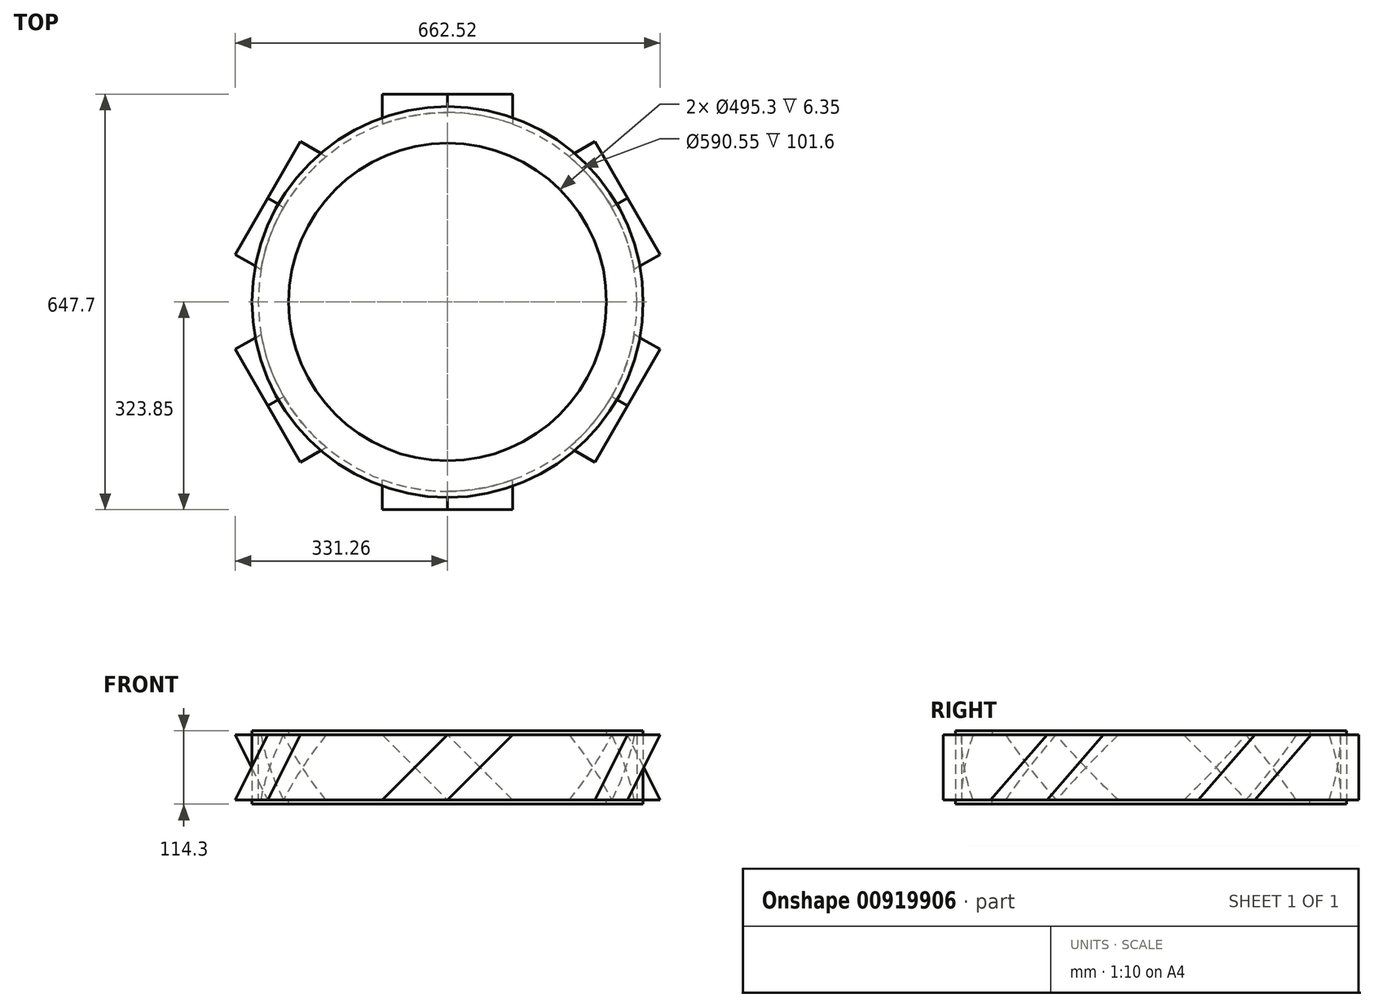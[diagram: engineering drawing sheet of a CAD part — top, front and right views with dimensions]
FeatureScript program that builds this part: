
annotation { "Feature Type Name" : "Feature", "Feature Type Description" : "" }
export const myFeature = defineFeature(function(context is Context, id is Id, definition is map)
    precondition{}
    {
        {
            var Q0;
            Q0=qCreatedBy(makeId("Top.planeOp"),FACE);
            var sketch = newSketch(context, id + "F0", { "sketchPlane" : qUnion([Q0])});
            skCircle(sketch, "E0", {"center": v(0, 0) * mm, "radius": 304.8 * mm});
            skCircle(sketch, "E1", {"center": v(0, 0) * mm, "radius": 295.28 * mm});
            skLineSegment(sketch, "E2", {"start": v(-528.88, -206.99) * mm, "end": v(-528.88, 98.57) * mm});
            skLineSegment(sketch, "E3", {"start": v(-528.88, 98.57) * mm, "end": v(-565.97, 49.3) * mm});
            skLineSegment(sketch, "E4", {"start": v(-565.97, 49.3) * mm, "end": v(-528.88, 98.57) * mm});
            skLineSegment(sketch, "E5", {"start": v(-528.88, 98.57) * mm, "end": v(-477.58, 49.3) * mm});
            skSolve(sketch);
        }
        {
            var Q0;
            Q0=makeQuery(id+"F0.imprint","IMPRINT",FACE,{"disambiguationData":[TD([[makeQuery(id+"F0.imprint","IMPRINT",EDGE,{"derivedFrom":sQuery(id+"F0.wireOp",EDGE,"E0")}),1.0]])]});
            extrude(context, id + "F1", {"entities" : qUnion([Q0]), "depth" : 101.6 * mm, "offsetDistance" : 25.4 * mm});
        }
        {
            var Q0;
            Q0=qCreatedBy(makeId("Front.planeOp"),FACE);
            var sketch = newSketch(context, id + "F2", { "sketchPlane" : qUnion([Q0])});
            skLineSegment(sketch, "E6", {"start": v(0, 0) * mm, "end": v(101.6, 0) * mm});
            skLineSegment(sketch, "E7", {"start": v(101.6, 0) * mm, "end": v(0, 101.6) * mm});
            skLineSegment(sketch, "E8", {"start": v(0, 101.6) * mm, "end": v(-101.6, 101.6) * mm});
            skLineSegment(sketch, "E9", {"start": v(-101.6, 101.6) * mm, "end": v(0, 0) * mm});
            skLineSegment(sketch, "E10", {"start": v(0, 101.6) * mm, "end": v(0, 0) * mm});
            skSolve(sketch);
        }
        {
            var Q0;
            Q0=makeQuery(id+"F2.imprint","IMPRINT",FACE,{"disambiguationData":[TD([[makeQuery(id+"F2.imprint","IMPRINT",EDGE,{"derivedFrom":sQuery(id+"F2.wireOp",EDGE,"E6")}),1.0]])]});
            var Q1;
            Q1=makeQuery(id+"F2.imprint","IMPRINT",FACE,{"disambiguationData":[TD([[makeQuery(id+"F2.imprint","IMPRINT",EDGE,{"derivedFrom":sQuery(id+"F2.wireOp",EDGE,"E8")}),1.0]])]});
            extrude(context, id + "F3", {"entities" : qUnion([Q0, Q1]), "oppositeDirection" : true, "depth" : 323.85 * mm, "offsetDistance" : 25.4 * mm});
        }
        {
            var Q0;
            Q0=makeQuery(id+"F0.imprint","IMPRINT",FACE,{"disambiguationData":[TD([[makeQuery(id+"F0.imprint","IMPRINT",EDGE,{"derivedFrom":sQuery(id+"F0.wireOp",EDGE,"E1")}),1.0]])]});
            extrude(context, id + "F4", {"entities" : qUnion([Q0]), "operationType" : NewBodyOperationType.REMOVE, "depth" : 254 * mm, "offsetDistance" : 25.4 * mm});
        }
        {
            var Q0;
            Q0=makeQuery(id+"F3.opExtrude","SWEPT_BODY",BODY,{"disambiguationData":[OSD([sQuery(id+"F2.wireOp",EDGE,"E6"),sQuery(id+"F2.wireOp",EDGE,"E7"),sQuery(id+"F2.wireOp",EDGE,"E8"),sQuery(id+"F2.wireOp",EDGE,"E9")])]});
            var Q1;
            Q1=sQuery(id+"F2.wireOp",EDGE,"E10");
            circularPattern(context, id + "F5", {"entities" : qUnion([Q0]), "axis" : qUnion([Q1]), "angle" : 360 * degree, "instanceCount" : 6, "equalSpace" : true});
        }
        {
            var Q0;
            Q0=makeQuery(id+"F0.imprint","IMPRINT",FACE,{"disambiguationData":[TD([[makeQuery(id+"F0.imprint","IMPRINT",EDGE,{"derivedFrom":sQuery(id+"F0.wireOp",EDGE,"E0")}),1.0]])]});
            var Q1;
            Q1=makeQuery(id+"F5.opPattern","COPY",FACE,{"derivedFrom":makeQuery(id+"F3.opExtrude","SWEPT_FACE",FACE,{"disambiguationData":[OSD([sQuery(id+"F2.wireOp",EDGE,"fI1UZwbh-BgUO-eOab-QM0r-AAAHP5eAAkyZ")])]}),"instanceName":"7"});
            var Q2;
            Q2=makeQuery(id+"F5.opPattern","COPY",FACE,{"derivedFrom":makeQuery(id+"F3.opExtrude","SWEPT_FACE",FACE,{"disambiguationData":[OSD([sQuery(id+"F2.wireOp",EDGE,"fI1UZwbh-BgUO-eOab-QM0r-AAAHP5eAAkyZ")])]}),"instanceName":"6"});
            var Q3;
            Q3=makeQuery(id+"F5.opPattern","COPY",FACE,{"derivedFrom":makeQuery(id+"F3.opExtrude","SWEPT_FACE",FACE,{"disambiguationData":[OSD([sQuery(id+"F2.wireOp",EDGE,"fI1UZwbh-BgUO-eOab-QM0r-AAAHP5eAAkyZ")])]}),"instanceName":"5"});
            var Q4;
            Q4=makeQuery(id+"F5.opPattern","COPY",FACE,{"derivedFrom":makeQuery(id+"F3.opExtrude","SWEPT_FACE",FACE,{"disambiguationData":[OSD([sQuery(id+"F2.wireOp",EDGE,"fI1UZwbh-BgUO-eOab-QM0r-AAAHP5eAAkyZ")])]}),"instanceName":"4"});
            var Q5;
            Q5=makeQuery(id+"F3.opExtrude","SWEPT_FACE",FACE,{"disambiguationData":[OSD([sQuery(id+"F2.wireOp",EDGE,"fI1UZwbh-BgUO-eOab-QM0r-AAAHP5eAAkyZ")])]});
            var Q6;
            Q6=makeQuery(id+"F5.opPattern","COPY",FACE,{"derivedFrom":makeQuery(id+"F3.opExtrude","SWEPT_FACE",FACE,{"disambiguationData":[OSD([sQuery(id+"F2.wireOp",EDGE,"fI1UZwbh-BgUO-eOab-QM0r-AAAHP5eAAkyZ")])]}),"instanceName":"1"});
            var Q7;
            Q7=makeQuery(id+"F5.opPattern","COPY",FACE,{"derivedFrom":makeQuery(id+"F3.opExtrude","SWEPT_FACE",FACE,{"disambiguationData":[OSD([sQuery(id+"F2.wireOp",EDGE,"fI1UZwbh-BgUO-eOab-QM0r-AAAHP5eAAkyZ")])]}),"instanceName":"2"});
            var Q8;
            Q8=makeQuery(id+"F5.opPattern","COPY",FACE,{"derivedFrom":makeQuery(id+"F3.opExtrude","SWEPT_FACE",FACE,{"disambiguationData":[OSD([sQuery(id+"F2.wireOp",EDGE,"fI1UZwbh-BgUO-eOab-QM0r-AAAHP5eAAkyZ")])]}),"instanceName":"3"});
            var Q9;
            Q9=makeQuery(id+"F0.imprint","IMPRINT",FACE,{"disambiguationData":[TD([[makeQuery(id+"F0.imprint","IMPRINT",EDGE,{"derivedFrom":sQuery(id+"F0.wireOp",EDGE,"E1")}),1.0]])]});
            extrude(context, id + "F6", {"entities" : qUnion([Q0, Q1, Q2, Q3, Q4, Q5, Q6, Q7, Q8, Q9]), "oppositeDirection" : true, "depth" : 6.35 * mm, "offsetDistance" : 25.4 * mm});
        }
        {
            var Q0;
            Q0=makeQuery(id+"F1.opExtrude","CAP_FACE",FACE,{"disambiguationData":[OSD([sQuery(id+"F0.wireOp",EDGE,"E0"),sQuery(id+"F0.wireOp",EDGE,"E1")])],"isStart":false});
            var sketch = newSketch(context, id + "F7", { "sketchPlane" : qUnion([Q0])});
            skCircle(sketch, "E11", {"center": v(0, 0) * mm, "radius": 247.65 * mm});
            skCircle(sketch, "E12", {"center": v(0, 0) * mm, "radius": 304.8 * mm});
            skSolve(sketch);
        }
        {
            var Q0;
            Q0=makeQuery(id+"F7.imprint","IMPRINT",FACE,{"disambiguationData":[TD([[makeQuery(id+"F7.imprint","IMPRINT",EDGE,{"derivedFrom":sQuery(id+"F7.wireOp",EDGE,"E11")}),-1.0]])]});
            var Q1;
            Q1=makeQuery(id+"F7.imprint","IMPRINT",FACE,{"disambiguationData":[TD([[makeQuery(id+"F7.imprint","IMPRINT",EDGE,{"derivedFrom":sQuery(id+"F7.wireOp",EDGE,"E12")}),1.0]])]});
            var Q2;
            Q2=makeQuery(id+"F5.opPattern","COPY",FACE,{"derivedFrom":makeQuery(id+"F3.opExtrude","SWEPT_FACE",FACE,{"disambiguationData":[OSD([sQuery(id+"F2.wireOp",EDGE,"ouPGAYGL-9uzs-f7dU-DYR0-UCYUhEhHpE3X")])]}),"instanceName":"6"});
            var Q3;
            Q3=makeQuery(id+"F5.opPattern","COPY",FACE,{"derivedFrom":makeQuery(id+"F3.opExtrude","SWEPT_FACE",FACE,{"disambiguationData":[OSD([sQuery(id+"F2.wireOp",EDGE,"ouPGAYGL-9uzs-f7dU-DYR0-UCYUhEhHpE3X")])]}),"instanceName":"5"});
            var Q4;
            Q4=makeQuery(id+"F5.opPattern","COPY",FACE,{"derivedFrom":makeQuery(id+"F3.opExtrude","SWEPT_FACE",FACE,{"disambiguationData":[OSD([sQuery(id+"F2.wireOp",EDGE,"ouPGAYGL-9uzs-f7dU-DYR0-UCYUhEhHpE3X")])]}),"instanceName":"3"});
            var Q5;
            Q5=makeQuery(id+"F5.opPattern","COPY",FACE,{"derivedFrom":makeQuery(id+"F3.opExtrude","SWEPT_FACE",FACE,{"disambiguationData":[OSD([sQuery(id+"F2.wireOp",EDGE,"ouPGAYGL-9uzs-f7dU-DYR0-UCYUhEhHpE3X")])]}),"instanceName":"2"});
            var Q6;
            Q6=makeQuery(id+"F3.opExtrude","SWEPT_FACE",FACE,{"disambiguationData":[OSD([sQuery(id+"F2.wireOp",EDGE,"ouPGAYGL-9uzs-f7dU-DYR0-UCYUhEhHpE3X")])]});
            var Q7;
            Q7=makeQuery(id+"F5.opPattern","COPY",FACE,{"derivedFrom":makeQuery(id+"F3.opExtrude","SWEPT_FACE",FACE,{"disambiguationData":[OSD([sQuery(id+"F2.wireOp",EDGE,"ouPGAYGL-9uzs-f7dU-DYR0-UCYUhEhHpE3X")])]}),"instanceName":"7"});
            var Q8;
            Q8=makeQuery(id+"F5.opPattern","COPY",FACE,{"derivedFrom":makeQuery(id+"F3.opExtrude","SWEPT_FACE",FACE,{"disambiguationData":[OSD([sQuery(id+"F2.wireOp",EDGE,"ouPGAYGL-9uzs-f7dU-DYR0-UCYUhEhHpE3X")])]}),"instanceName":"1"});
            var Q9;
            Q9=makeQuery(id+"F5.opPattern","COPY",FACE,{"derivedFrom":makeQuery(id+"F3.opExtrude","SWEPT_FACE",FACE,{"disambiguationData":[OSD([sQuery(id+"F2.wireOp",EDGE,"ouPGAYGL-9uzs-f7dU-DYR0-UCYUhEhHpE3X")])]}),"instanceName":"4"});
            extrude(context, id + "F8", {"entities" : qUnion([Q0, Q1, Q2, Q3, Q4, Q5, Q6, Q7, Q8, Q9]), "depth" : 6.35 * mm, "offsetDistance" : 25.4 * mm});
        }
        {
            var Q0;
            Q0=makeQuery(id+"F7.imprint","IMPRINT",FACE,{"disambiguationData":[TD([[makeQuery(id+"F7.imprint","IMPRINT",EDGE,{"derivedFrom":sQuery(id+"F7.wireOp",EDGE,"E11")}),1.0]])]});
            extrude(context, id + "F9", {"entities" : qUnion([Q0]), "operationType" : NewBodyOperationType.REMOVE, "oppositeDirection" : true, "depth" : 127 * mm, "offsetDistance" : 25.4 * mm});
        }
    });
